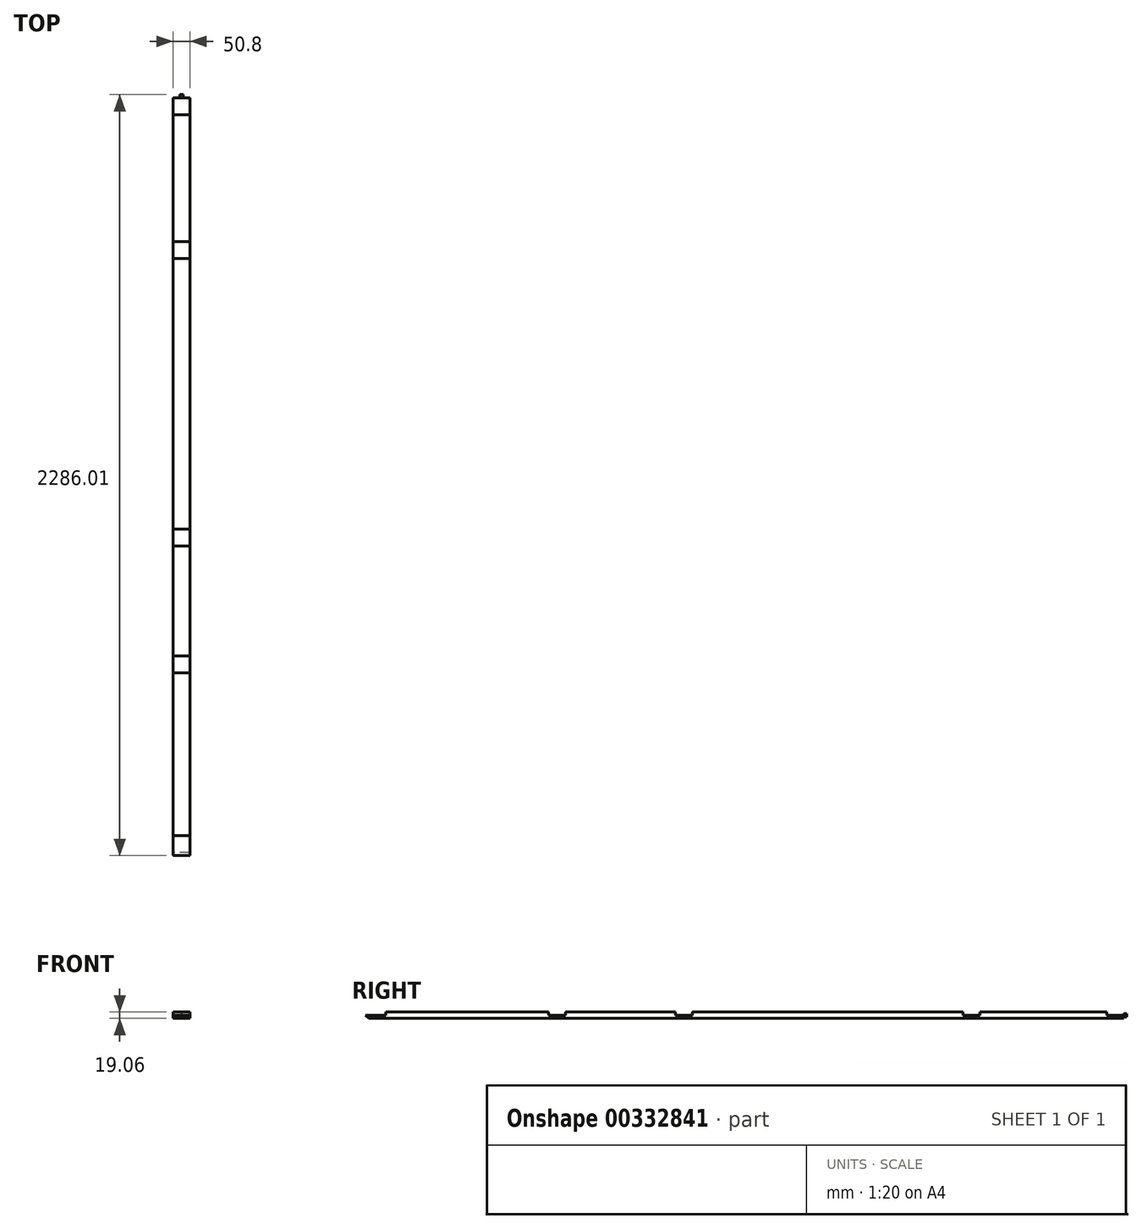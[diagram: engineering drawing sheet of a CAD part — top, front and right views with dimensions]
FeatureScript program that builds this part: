
annotation { "Feature Type Name" : "Feature", "Feature Type Description" : "" }
export const myFeature = defineFeature(function(context is Context, id is Id, definition is map)
    precondition{}
    {
        {
            var Q0;
            Q0=qCreatedBy(makeId("Right.planeOp"),FACE);
            var sketch = newSketch(context, id + "F0", { "sketchPlane" : qUnion([Q0])});
            skLineSegment(sketch, "E0.top", {"start": v(2133.6, -9.52) * mm, "end": v(2133.6, 0) * mm});
            skLineSegment(sketch, "E0.right", {"start": v(0, 9.52) * mm, "end": v(406.4, 9.53) * mm});
            skLineSegment(sketch, "E1.top", {"start": v(2082.8, 9.53) * mm, "end": v(2082.8, 0) * mm});
            skLineSegment(sketch, "E1.right", {"start": v(2133.6, 0) * mm, "end": v(2082.8, 0) * mm});
            skLineSegment(sketch, "E2", {"start": v(2133.6, -9.52) * mm, "end": v(-33.3, -9.53) * mm});
            skLineSegment(sketch, "E3.right", {"start": v(2082.8, 0) * mm, "end": v(2082.8, 0) * mm});
            skLineSegment(sketch, "E4.trimOffspring", {"start": v(2082.8, 9.53) * mm, "end": v(2082.8, 9.53) * mm});
            skLineSegment(sketch, "E5.top", {"start": v(1651, 9.53) * mm, "end": v(1651, 0) * mm});
            skLineSegment(sketch, "E5.right", {"start": v(1701.8, 0) * mm, "end": v(1651, 0) * mm});
            skLineSegment(sketch, "E6.bottom", {"start": v(838.2, 9.53) * mm, "end": v(838.2, 0) * mm});
            skLineSegment(sketch, "E6.top", {"start": v(787.4, 9.53) * mm, "end": v(787.4, 0) * mm});
            skLineSegment(sketch, "E6.right", {"start": v(838.2, 0) * mm, "end": v(787.4, 0) * mm});
            skPoint(sketch, "E6.left.start.orphan", {"position": v(838.2, 48.5) * mm});
            skPoint(sketch, "E7.orphan", {"position": v(787.4, 48.5) * mm});
            skLineSegment(sketch, "E8.trimOffspring", {"start": v(838.2, 9.53) * mm, "end": v(1651, 9.53) * mm});
            skLineSegment(sketch, "E9", {"start": v(1701.8, 0) * mm, "end": v(1701.8, 9.53) * mm});
            skLineSegment(sketch, "E10.trimOffspring", {"start": v(1701.8, 9.53) * mm, "end": v(2082.8, 9.53) * mm});
            skLineSegment(sketch, "E11", {"start": v(0, 9.52) * mm, "end": v(-82.55, 9.52) * mm});
            skLineSegment(sketch, "E12", {"start": v(-142.88, 0) * mm, "end": v(-133.35, -9.53) * mm});
            skLineSegment(sketch, "E13", {"start": v(-33.3, -9.53) * mm, "end": v(-133.35, -9.53) * mm});
            skPoint(sketch, "E14.start.orphan", {"position": v(431.8, 9.53) * mm});
            skLineSegment(sketch, "E15.top", {"start": v(406.4, 0) * mm, "end": v(457.2, 0) * mm});
            skLineSegment(sketch, "E15.left", {"start": v(406.4, 9.53) * mm, "end": v(406.4, 0) * mm});
            skLineSegment(sketch, "E15.right", {"start": v(457.2, 9.53) * mm, "end": v(457.2, 0) * mm});
            skLineSegment(sketch, "E16.trimOffspring", {"start": v(457.2, 9.53) * mm, "end": v(787.4, 9.53) * mm});
            skLineSegment(sketch, "E17.top", {"start": v(-142.88, 0) * mm, "end": v(-82.55, 0) * mm});
            skLineSegment(sketch, "E17.right", {"start": v(-82.55, 9.52) * mm, "end": v(-82.55, 0) * mm});
            skPoint(sketch, "E18.orphan", {"position": v(-152.4, 9.52) * mm});
            skSolve(sketch);
        }
        {
            var Q0;
            Q0=qSketchRegion(id+"F0",true);
            extrude(context, id + "F1", {"entities" : qUnion([Q0]), "endBound" : BoundingType.SYMMETRIC, "depth" : 50.8 * mm});
        }
        {
            var Q0;
            Q0=qCreatedBy(makeId("Front.planeOp"),FACE);
            cPlane(context, id + "F2", {"entities" : qUnion([Q0]), "cplaneType" : CPlaneType.OFFSET, "offset" : 2133.6 * mm, "oppositeDirection" : true, "width" : 152.4 * mm, "height" : 152.4 * mm});
        }
        {
            var Q0;
            Q0=qCreatedBy(id+"F2.planeOp",FACE);
            var sketch = newSketch(context, id + "F3", { "sketchPlane" : qUnion([Q0])});
            skCircle(sketch, "E19", {"center": v(0, 0) * mm, "radius": 4.76 * mm});
            skSolve(sketch);
        }
        {
            var Q0;
            Q0=qSketchRegion(id+"F3",true);
            extrude(context, id + "F4", {"entities" : qUnion([Q0]), "operationType" : NewBodyOperationType.ADD, "oppositeDirection" : true, "depth" : 9.52 * mm});
        }
    });
